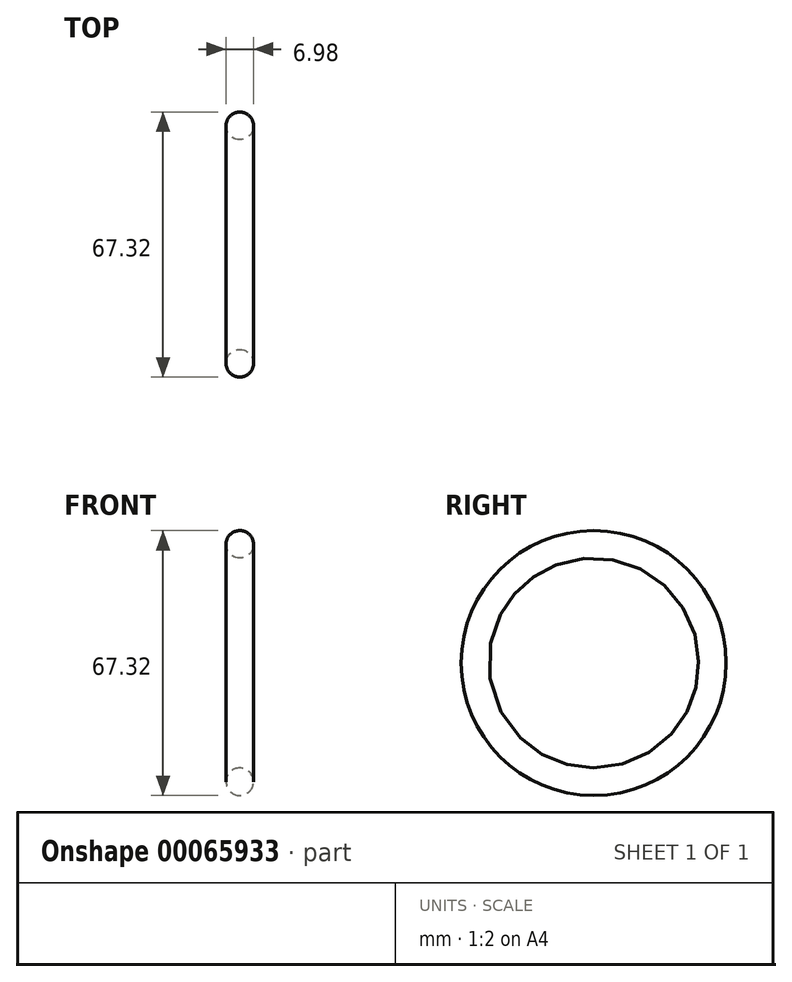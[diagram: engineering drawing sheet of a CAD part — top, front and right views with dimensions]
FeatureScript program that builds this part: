
annotation { "Feature Type Name" : "Feature", "Feature Type Description" : "" }
export const myFeature = defineFeature(function(context is Context, id is Id, definition is map)
    precondition{}
    {
        {
            var Q0;
            Q0=qCreatedBy(makeId("Front.planeOp"),FACE);
            var sketch = newSketch(context, id + "F0", { "sketchPlane" : qUnion([Q0])});
            skLineSegment(sketch, "E0", {"start": v(0, 0) * mm, "end": v(-6.06, 0) * mm, "construction": true});
            skCircle(sketch, "E1", {"center": v(0, 30.16) * mm, "radius": 3.5 * mm});
            skSolve(sketch);
        }
        {
            var Q0;
            Q0=makeQuery(id+"F0.imprint","IMPRINT",FACE,{"disambiguationData":[TD([[makeQuery(id+"F0.imprint","IMPRINT",EDGE,{"derivedFrom":sQuery(id+"F0.wireOp",EDGE,"E1")}),1.0]])]});
            var Q1;
            Q1=sQuery(id+"F0.wireOp",EDGE,"E0");
            revolve(context, id + "F1", {"entities" : qUnion([Q0]), "axis" : qUnion([Q1]), "revolveType" : RevolveType.FULL});
        }
    });
